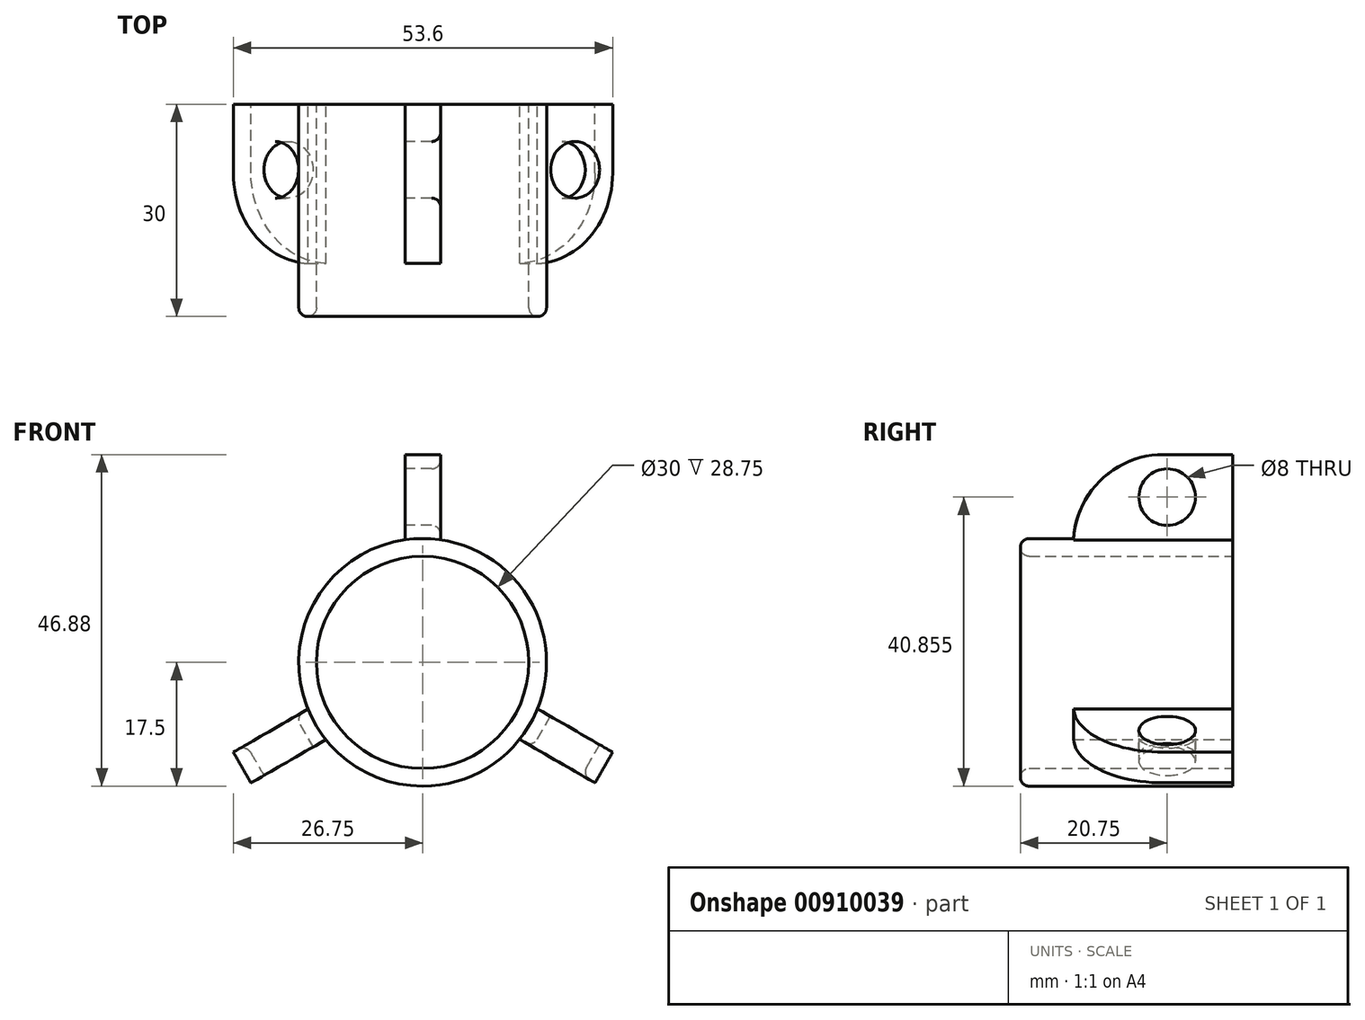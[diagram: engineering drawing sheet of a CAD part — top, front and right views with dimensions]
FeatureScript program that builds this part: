
annotation { "Feature Type Name" : "Feature", "Feature Type Description" : "" }
export const myFeature = defineFeature(function(context is Context, id is Id, definition is map)
    precondition{}
    {
        {
            var Q0;
            Q0=qCreatedBy(makeId("Front.planeOp"),FACE);
            var sketch = newSketch(context, id + "F0", { "sketchPlane" : qUnion([Q0])});
            skCircle(sketch, "E0", {"center": v(0, 0) * mm, "radius": 17.5 * mm});
            skCircle(sketch, "E1", {"center": v(0, 0) * mm, "radius": 15 * mm});
            skSolve(sketch);
        }
        {
            var Q0;
            Q0 = qSketchRegion(id + "F0", true);
            extrude(context, id + "F1", {"entities" : qUnion([Q0]), "depth" : 30 * mm, "offsetDistance" : 25 * mm});
        }
        {
            var Q0;
            Q0=qCreatedBy(makeId("Front.planeOp"),FACE);
            var sketch = newSketch(context, id + "F2", { "sketchPlane" : qUnion([Q0])});
            skLineSegment(sketch, "E2.bottom", {"start": v(24.35, -17.03) * mm, "end": v(26.85, -12.7) * mm});
            skLineSegment(sketch, "E2.top", {"start": v(3.56, -5.03) * mm, "end": v(6.06, -0.7) * mm});
            skLineSegment(sketch, "E2.left", {"start": v(24.35, -17.03) * mm, "end": v(3.56, -5.03) * mm});
            skLineSegment(sketch, "E2.right", {"start": v(26.85, -12.7) * mm, "end": v(6.06, -0.7) * mm});
            skPoint(sketch, "E2.middle", {"position": v(15.2, -8.87) * mm});
            skLineSegment(sketch, "E3.bottom", {"start": v(-26.75, -12.7) * mm, "end": v(-24.25, -17.03) * mm});
            skLineSegment(sketch, "E3.top", {"start": v(-5.96, -0.7) * mm, "end": v(-3.46, -5.03) * mm});
            skLineSegment(sketch, "E3.left", {"start": v(-26.75, -12.7) * mm, "end": v(-5.96, -0.7) * mm});
            skLineSegment(sketch, "E3.right", {"start": v(-24.25, -17.03) * mm, "end": v(-3.46, -5.03) * mm});
            skPoint(sketch, "E3.middle", {"position": v(-15.1, -8.87) * mm});
            skLineSegment(sketch, "E4.bottom", {"start": v(2.55, 29.38) * mm, "end": v(-2.45, 29.38) * mm});
            skLineSegment(sketch, "E4.top", {"start": v(2.55, 5.38) * mm, "end": v(-2.45, 5.38) * mm});
            skLineSegment(sketch, "E4.left", {"start": v(2.55, 29.38) * mm, "end": v(2.55, 5.38) * mm});
            skLineSegment(sketch, "E4.right", {"start": v(-2.45, 29.38) * mm, "end": v(-2.45, 5.38) * mm});
            skPoint(sketch, "E4.middle", {"position": v(0.05, 17.38) * mm});
            skCircle(sketch, "E5", {"center": v(0, 0) * mm, "radius": 16.22 * mm});
            skSolve(sketch);
        }
        {
            var Q0;
            Q0=makeQuery(id+"F1.opExtrude","CAP_EDGE",EDGE,{"disambiguationData":[OSD([sQuery(id+"F0.wireOp",EDGE,"E1")])],"isStart":false});
            var Q1;
            Q1=makeQuery(id+"F1.opExtrude","CAP_EDGE",EDGE,{"disambiguationData":[OSD([sQuery(id+"F0.wireOp",EDGE,"E0")])],"isStart":false});
            fillet(context, id + "F3", {"entities" : qUnion([Q0, Q1]), "radius" : 1.25 * mm, "tangentPropagation" : true, "allowEdgeOverflow" : false});
        }
        {
            var Q0;
            Q0 = qSketchRegion(id + "F2", true);
            extrude(context, id + "F4", {"entities" : qUnion([Q0]), "operationType" : NewBodyOperationType.ADD, "depth" : 22.5 * mm, "offsetDistance" : 25 * mm});
        }
        {
            var Q0;
            Q0=makeQuery(id+"F4.boolean.opBoolean","SPLIT",FACE,{"disambiguationData":[TD([makeQuery(id+"F1.opExtrude","SWEPT_FACE",FACE,{"disambiguationData":[OSD([sQuery(id+"F0.wireOp",EDGE,"E1")])]})])],"derivedFrom":makeQuery(id+"F4.opExtrude","CAP_FACE",FACE,{"disambiguationData":[OSD([sQuery(id+"F2.wireOp",EDGE,"E2.bottom"),sQuery(id+"F2.wireOp",EDGE,"E2.left"),sQuery(id+"F2.wireOp",EDGE,"E2.right"),sQuery(id+"F2.wireOp",EDGE,"E3.bottom"),sQuery(id+"F2.wireOp",EDGE,"E3.left"),sQuery(id+"F2.wireOp",EDGE,"E3.right"),sQuery(id+"F2.wireOp",EDGE,"E4.bottom"),sQuery(id+"F2.wireOp",EDGE,"E4.left"),sQuery(id+"F2.wireOp",EDGE,"E4.right"),sQuery(id+"F2.wireOp",EDGE,"E5")])],"isStart":false})});
            extrude(context, id + "F5", {"entities" : qUnion([Q0]), "operationType" : NewBodyOperationType.REMOVE, "oppositeDirection" : true, "depth" : 25 * mm, "offsetDistance" : 25 * mm});
        }
        {
            var Q0;
            Q0=makeQuery(id+"F4.opExtrude","SWEPT_FACE",FACE,{"disambiguationData":[OSD([sQuery(id+"F2.wireOp",EDGE,"E3.right")])]});
            var sketch = newSketch(context, id + "F6", { "sketchPlane" : qUnion([Q0])});
            skPoint(sketch, "E6.endSnap0", {"position": v(-23.4, 22.5) * mm});
            skCircle(sketch, "E7", {"center": v(-23.4, 9.25) * mm, "radius": 4 * mm});
            skSolve(sketch);
        }
        {
            var Q0;
            Q0 = qSketchRegion(id + "F6", true);
            extrude(context, id + "F7", {"entities" : qUnion([Q0]), "operationType" : NewBodyOperationType.REMOVE, "oppositeDirection" : true, "depth" : 25 * mm, "offsetDistance" : 25 * mm});
        }
        {
            var Q0;
            Q0=makeQuery(id+"F4.opExtrude","SWEPT_FACE",FACE,{"disambiguationData":[OSD([sQuery(id+"F2.wireOp",EDGE,"E2.right")])]});
            var sketch = newSketch(context, id + "F8", { "sketchPlane" : qUnion([Q0])});
            skCircle(sketch, "E8", {"center": v(23.47, -9.25) * mm, "radius": 4 * mm});
            skSolve(sketch);
        }
        {
            var Q0;
            Q0 = qSketchRegion(id + "F8", true);
            extrude(context, id + "F9", {"entities" : qUnion([Q0]), "operationType" : NewBodyOperationType.REMOVE, "oppositeDirection" : true, "depth" : 25 * mm, "offsetDistance" : 25 * mm});
        }
        {
            var Q0;
            Q0=makeQuery(id+"F4.opExtrude","SWEPT_FACE",FACE,{"disambiguationData":[OSD([sQuery(id+"F2.wireOp",EDGE,"E4.right")])]});
            var sketch = newSketch(context, id + "F10", { "sketchPlane" : qUnion([Q0])});
            skCircle(sketch, "E9", {"center": v(9.25, 23.35) * mm, "radius": 4 * mm});
            skSolve(sketch);
        }
        {
            var Q0;
            Q0 = qSketchRegion(id + "F10", true);
            extrude(context, id + "F11", {"entities" : qUnion([Q0]), "operationType" : NewBodyOperationType.REMOVE, "oppositeDirection" : true, "depth" : 25 * mm, "offsetDistance" : 25 * mm});
        }
        {
            var Q0;
            Q0=makeQuery(id+"F9.boolean.opBoolean","COPY",EDGE,{"derivedFrom":makeQuery(id+"F9.opExtrude","CAP_EDGE",EDGE,{"disambiguationData":[OSD([sQuery(id+"F8.wireOp",EDGE,"E8")])],"isStart":true})});
            var Q1;
            Q1=makeQuery(id+"F9.boolean.opBoolean","INTERSECT",EDGE,{"derivedFrom":[makeQuery(id+"F4.opExtrude","SWEPT_FACE",FACE,{"disambiguationData":[OSD([sQuery(id+"F2.wireOp",EDGE,"E2.left")])]}),makeQuery(id+"F9.opExtrude","SWEPT_FACE",FACE,{"disambiguationData":[OSD([sQuery(id+"F8.wireOp",EDGE,"E8")])]})]});
            var Q2;
            Q2=makeQuery(id+"F7.boolean.opBoolean","INTERSECT",EDGE,{"derivedFrom":[makeQuery(id+"F4.opExtrude","SWEPT_FACE",FACE,{"disambiguationData":[OSD([sQuery(id+"F2.wireOp",EDGE,"E3.left")])]}),makeQuery(id+"F7.opExtrude","SWEPT_FACE",FACE,{"disambiguationData":[OSD([sQuery(id+"F6.wireOp",EDGE,"E7")])]})]});
            var Q3;
            Q3=makeQuery(id+"F7.boolean.opBoolean","COPY",EDGE,{"derivedFrom":makeQuery(id+"F7.opExtrude","CAP_EDGE",EDGE,{"disambiguationData":[OSD([sQuery(id+"F6.wireOp",EDGE,"E7")])],"isStart":true})});
            var Q4;
            Q4=makeQuery(id+"F11.boolean.opBoolean","COPY",EDGE,{"derivedFrom":makeQuery(id+"F11.opExtrude","CAP_EDGE",EDGE,{"disambiguationData":[OSD([sQuery(id+"F10.wireOp",EDGE,"E9")])],"isStart":true})});
            var Q5;
            Q5=makeQuery(id+"F11.boolean.opBoolean","INTERSECT",EDGE,{"derivedFrom":[makeQuery(id+"F4.opExtrude","SWEPT_FACE",FACE,{"disambiguationData":[OSD([sQuery(id+"F2.wireOp",EDGE,"E4.left")])]}),makeQuery(id+"F11.opExtrude","SWEPT_FACE",FACE,{"disambiguationData":[OSD([sQuery(id+"F10.wireOp",EDGE,"E9")])]})]});
            fillet(context, id + "F12", {"entities" : qUnion([Q0, Q1, Q2, Q3, Q4, Q5]), "radius" : 1.3 * mm, "allowEdgeOverflow" : false});
        }
        {
            var Q0;
            Q0=makeQuery(id+"F4.opExtrude","CAP_EDGE",EDGE,{"disambiguationData":[OSD([sQuery(id+"F2.wireOp",EDGE,"E4.bottom")])],"isStart":false});
            var Q1;
            Q1=makeQuery(id+"F4.opExtrude","CAP_EDGE",EDGE,{"disambiguationData":[OSD([sQuery(id+"F2.wireOp",EDGE,"E3.bottom")])],"isStart":false});
            var Q2;
            Q2=makeQuery(id+"F4.opExtrude","CAP_EDGE",EDGE,{"disambiguationData":[OSD([sQuery(id+"F2.wireOp",EDGE,"E2.bottom")])],"isStart":false});
            fillet(context, id + "F13", {"entities" : qUnion([Q0, Q1, Q2]), "radius" : 12.8 * mm, "tangentPropagation" : true, "allowEdgeOverflow" : false});
        }
    });
